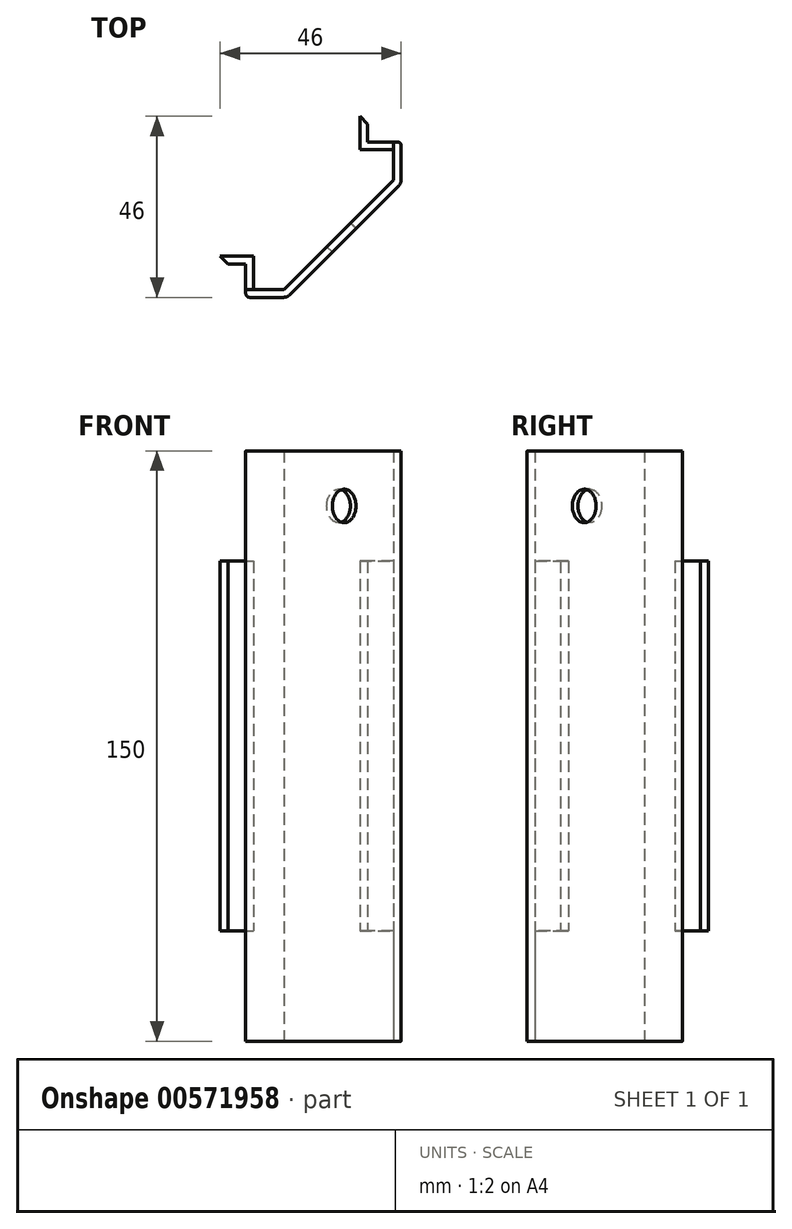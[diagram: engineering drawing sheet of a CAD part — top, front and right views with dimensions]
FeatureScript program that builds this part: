
annotation { "Feature Type Name" : "Feature", "Feature Type Description" : "" }
export const myFeature = defineFeature(function(context is Context, id is Id, definition is map)
    precondition{}
    {
        {
            var Q0;
            Q0=qCreatedBy(makeId("Top.planeOp"),FACE);
            var sketch = newSketch(context, id + "F0", { "sketchPlane" : qUnion([Q0])});
            skLineSegment(sketch, "E0", {"start": v(-68.1, 0) * mm, "end": v(72.16, 0) * mm, "construction": true});
            skLineSegment(sketch, "E1", {"start": v(0, 70.28) * mm, "end": v(0, -61.88) * mm, "construction": true});
            skLineSegment(sketch, "E2.bottom", {"start": v(-19.75, 19.75) * mm, "end": v(19.75, 19.75) * mm, "construction": true});
            skLineSegment(sketch, "E2.top", {"start": v(-19.75, -19.75) * mm, "end": v(19.75, -19.75) * mm, "construction": true});
            skLineSegment(sketch, "E2.left", {"start": v(-19.75, 19.75) * mm, "end": v(-19.75, -19.75) * mm, "construction": true});
            skLineSegment(sketch, "E2.right", {"start": v(19.75, 19.75) * mm, "end": v(19.75, -19.75) * mm, "construction": true});
            skLineSegment(sketch, "E3", {"start": v(-19.75, -19.75) * mm, "end": v(-9.25, -19.75) * mm});
            skLineSegment(sketch, "E4", {"start": v(19.75, 19.75) * mm, "end": v(19.75, 9.25) * mm});
            skLineSegment(sketch, "E5", {"start": v(-9.25, -19.75) * mm, "end": v(19.75, 9.25) * mm});
            skLineSegment(sketch, "E6.0", {"start": v(-19.75, -17.75) * mm, "end": v(-10.08, -17.75) * mm});
            skLineSegment(sketch, "E6.1", {"start": v(-10.08, -17.75) * mm, "end": v(17.75, 10.08) * mm});
            skLineSegment(sketch, "E6.2", {"start": v(17.75, 19.75) * mm, "end": v(17.75, 10.08) * mm});
            skLineSegment(sketch, "E7", {"start": v(-19.75, -19.75) * mm, "end": v(-19.75, -17.75) * mm});
            skLineSegment(sketch, "E8", {"start": v(19.75, 19.75) * mm, "end": v(17.75, 19.75) * mm});
            skSolve(sketch);
        }
        {
            var Q0;
            Q0=qSketchRegion(id+"F0",true);
            extrude(context, id + "F1", {"entities" : qUnion([Q0]), "depth" : 28 * mm});
        }
        {
            var Q0;
            Q0=makeQuery(id+"F1.opExtrude","CAP_FACE",FACE,{"disambiguationData":[OSD([sQuery(id+"F0.wireOp",EDGE,"E3"),sQuery(id+"F0.wireOp",EDGE,"E4"),sQuery(id+"F0.wireOp",EDGE,"E5"),sQuery(id+"F0.wireOp",EDGE,"E6.0"),sQuery(id+"F0.wireOp",EDGE,"E6.1"),sQuery(id+"F0.wireOp",EDGE,"E6.2"),sQuery(id+"F0.wireOp",EDGE,"E7"),sQuery(id+"F0.wireOp",EDGE,"E8")])],"isStart":false});
            var sketch = newSketch(context, id + "F2", { "sketchPlane" : qUnion([Q0])});
            skLineSegment(sketch, "E9.1", {"start": v(-9.25, -19.75) * mm, "end": v(19.75, 9.25) * mm});
            skLineSegment(sketch, "E9.2", {"start": v(19.75, 19.75) * mm, "end": v(19.75, 9.25) * mm});
            skLineSegment(sketch, "E10", {"start": v(19.75, 19.75) * mm, "end": v(11.25, 19.75) * mm});
            skLineSegment(sketch, "E11", {"start": v(17.75, 17.75) * mm, "end": v(17.75, 10.08) * mm});
            skLineSegment(sketch, "E12", {"start": v(17.75, 10.08) * mm, "end": v(16.59, 8.91) * mm});
            skLineSegment(sketch, "E13.left", {"start": v(11.25, 19.75) * mm, "end": v(11.25, 24.25) * mm});
            skLineSegment(sketch, "E14", {"start": v(11.25, 24.25) * mm, "end": v(9.25, 26.25) * mm});
            skLineSegment(sketch, "E15.trimOffspring", {"start": v(16.59, 8.91) * mm, "end": v(-8.91, -16.59) * mm});
            skLineSegment(sketch, "E16.0", {"start": v(9.25, 19.75) * mm, "end": v(9.25, 23.42) * mm});
            skLineSegment(sketch, "E17.0", {"start": v(9.25, 23.42) * mm, "end": v(9.25, 23.42) * mm});
            skLineSegment(sketch, "E18.trimOffspring", {"start": v(9.25, 23.42) * mm, "end": v(9.25, 26.25) * mm});
            skLineSegment(sketch, "E19", {"start": v(0, 0) * mm, "end": v(5.25, -5.25) * mm, "construction": true});
            skLineSegment(sketch, "E20.MirrorCS", {"start": v(-19.75, -9.25) * mm, "end": v(-23.42, -9.25) * mm});
            skLineSegment(sketch, "E21.MirrorCS", {"start": v(-19.75, -11.25) * mm, "end": v(-24.25, -11.25) * mm});
            skLineSegment(sketch, "E22.MirrorCS", {"start": v(-23.42, -9.25) * mm, "end": v(-26.25, -9.25) * mm});
            skLineSegment(sketch, "E23.MirrorCS", {"start": v(-19.75, -19.75) * mm, "end": v(-9.25, -19.75) * mm});
            skLineSegment(sketch, "E24.MirrorCS", {"start": v(-10.08, -17.75) * mm, "end": v(-8.91, -16.59) * mm});
            skLineSegment(sketch, "E25.MirrorCS", {"start": v(-24.25, -11.25) * mm, "end": v(-26.25, -9.25) * mm});
            skLineSegment(sketch, "E26.MirrorCS", {"start": v(-17.75, -17.75) * mm, "end": v(-10.08, -17.75) * mm});
            skLineSegment(sketch, "E27.MirrorCS", {"start": v(-23.42, -9.25) * mm, "end": v(-23.42, -9.25) * mm});
            skLineSegment(sketch, "E28.MirrorCS", {"start": v(-19.75, -19.75) * mm, "end": v(-19.75, -11.25) * mm});
            skLineSegment(sketch, "E29.trimOffspring", {"start": v(-8.91, -16.59) * mm, "end": v(-10.08, -17.75) * mm});
            skLineSegment(sketch, "E30", {"start": v(9.25, 19.75) * mm, "end": v(9.25, 17.75) * mm});
            skLineSegment(sketch, "E31", {"start": v(9.25, 17.75) * mm, "end": v(17.75, 17.75) * mm});
            skLineSegment(sketch, "E32", {"start": v(-19.75, -9.25) * mm, "end": v(-17.75, -9.25) * mm});
            skLineSegment(sketch, "E33", {"start": v(-17.75, -9.25) * mm, "end": v(-17.75, -17.75) * mm});
            skSolve(sketch);
        }
        {
            var Q0;
            Q0=qSketchRegion(id+"F2",true);
            extrude(context, id + "F3", {"entities" : qUnion([Q0]), "operationType" : NewBodyOperationType.ADD, "depth" : 94 * mm, "offsetDistance" : 25 * mm});
        }
        {
            var Q0;
            Q0=makeQuery(id+"F3.opExtrude","CAP_FACE",FACE,{"disambiguationData":[OSD([sQuery(id+"F2.wireOp",EDGE,"E9.1"),sQuery(id+"F2.wireOp",EDGE,"E9.2"),sQuery(id+"F2.wireOp",EDGE,"E10"),sQuery(id+"F2.wireOp",EDGE,"E11"),sQuery(id+"F2.wireOp",EDGE,"E12"),sQuery(id+"F2.wireOp",EDGE,"E13.left"),sQuery(id+"F2.wireOp",EDGE,"E14"),sQuery(id+"F2.wireOp",EDGE,"E15.trimOffspring"),sQuery(id+"F2.wireOp",EDGE,"E16.0"),sQuery(id+"F2.wireOp",EDGE,"E17.0"),sQuery(id+"F2.wireOp",EDGE,"E18.trimOffspring"),sQuery(id+"F2.wireOp",EDGE,"E20.MirrorCS"),sQuery(id+"F2.wireOp",EDGE,"E21.MirrorCS"),sQuery(id+"F2.wireOp",EDGE,"E22.MirrorCS"),sQuery(id+"F2.wireOp",EDGE,"E23.MirrorCS"),sQuery(id+"F2.wireOp",EDGE,"E25.MirrorCS"),sQuery(id+"F2.wireOp",EDGE,"E26.MirrorCS"),sQuery(id+"F2.wireOp",EDGE,"E27.MirrorCS"),sQuery(id+"F2.wireOp",EDGE,"E28.MirrorCS"),sQuery(id+"F2.wireOp",EDGE,"E29.trimOffspring"),sQuery(id+"F2.wireOp",EDGE,"E30"),sQuery(id+"F2.wireOp",EDGE,"E31"),sQuery(id+"F2.wireOp",EDGE,"E32"),sQuery(id+"F2.wireOp",EDGE,"E33")])],"isStart":false});
            var sketch = newSketch(context, id + "F4", { "sketchPlane" : qUnion([Q0])});
            skLineSegment(sketch, "E34.0.0", {"start": v(19.75, 19.75) * mm, "end": v(19.75, 9.25) * mm});
            skLineSegment(sketch, "E34.0.1", {"start": v(19.75, 9.25) * mm, "end": v(-9.25, -19.75) * mm});
            skLineSegment(sketch, "E34.0.2", {"start": v(-9.25, -19.75) * mm, "end": v(-19.75, -19.75) * mm});
            skLineSegment(sketch, "E34.0.3", {"start": v(-19.75, -19.75) * mm, "end": v(-19.75, -17.75) * mm});
            skLineSegment(sketch, "E34.0.4", {"start": v(-19.75, -17.75) * mm, "end": v(-10.08, -17.75) * mm});
            skLineSegment(sketch, "E34.0.5", {"start": v(-10.08, -17.75) * mm, "end": v(17.75, 10.08) * mm});
            skLineSegment(sketch, "E34.0.6", {"start": v(17.75, 10.08) * mm, "end": v(17.75, 19.75) * mm});
            skLineSegment(sketch, "E34.0.7", {"start": v(17.75, 19.75) * mm, "end": v(19.75, 19.75) * mm});
            skSolve(sketch);
        }
        {
            var Q0;
            Q0=qSketchRegion(id+"F4",true);
            extrude(context, id + "F5", {"entities" : qUnion([Q0]), "operationType" : NewBodyOperationType.ADD, "depth" : 28 * mm});
        }
        {
            var Q0;
            Q0=makeQuery(id+"F5.boolean.opBoolean","MERGE",EDGE,{"derivedFrom":[makeQuery(id+"F3.boolean.opBoolean","MERGE",EDGE,{"derivedFrom":[makeQuery(id+"F1.opExtrude","SWEPT_EDGE",EDGE,{"disambiguationData":[OSD([sQuery(id+"F0.wireOp",EDGE,"E4"),sQuery(id+"F0.wireOp",EDGE,"E5")])]}),makeQuery(id+"F3.opExtrude","SWEPT_EDGE",EDGE,{"disambiguationData":[OSD([sQuery(id+"F2.wireOp",EDGE,"E9.1"),sQuery(id+"F2.wireOp",EDGE,"E9.2")])]})]}),makeQuery(id+"F5.opExtrude","SWEPT_EDGE",EDGE,{"disambiguationData":[OSD([sQuery(id+"F4.wireOp",EDGE,"E34.0.0"),sQuery(id+"F4.wireOp",EDGE,"E34.0.1")])]})]});
            var Q1;
            Q1=makeQuery(id+"F5.boolean.opBoolean","MERGE",EDGE,{"derivedFrom":[makeQuery(id+"F3.boolean.opBoolean","MERGE",EDGE,{"derivedFrom":[makeQuery(id+"F1.opExtrude","SWEPT_EDGE",EDGE,{"disambiguationData":[OSD([sQuery(id+"F0.wireOp",EDGE,"E3"),sQuery(id+"F0.wireOp",EDGE,"E5")])]}),makeQuery(id+"F3.opExtrude","SWEPT_EDGE",EDGE,{"disambiguationData":[OSD([sQuery(id+"F2.wireOp",EDGE,"E9.1"),sQuery(id+"F2.wireOp",EDGE,"E23.MirrorCS")])]})]}),makeQuery(id+"F5.opExtrude","SWEPT_EDGE",EDGE,{"disambiguationData":[OSD([sQuery(id+"F4.wireOp",EDGE,"E34.0.1"),sQuery(id+"F4.wireOp",EDGE,"E34.0.2")])]})]});
            fillet(context, id + "F6", {"entities" : qUnion([Q0, Q1]), "radius" : 2 * mm, "tangentPropagation" : true, "allowEdgeOverflow" : false});
        }
        {
            var Q0;
            Q0=makeQuery(id+"F5.boolean.opBoolean","MERGE",EDGE,{"derivedFrom":[makeQuery(id+"F3.boolean.opBoolean","MERGE",EDGE,{"derivedFrom":[makeQuery(id+"F1.opExtrude","SWEPT_EDGE",EDGE,{"disambiguationData":[OSD([sQuery(id+"F0.wireOp",EDGE,"E3"),sQuery(id+"F0.wireOp",EDGE,"E7")])]}),makeQuery(id+"F3.opExtrude","SWEPT_EDGE",EDGE,{"disambiguationData":[OSD([sQuery(id+"F2.wireOp",EDGE,"E23.MirrorCS"),sQuery(id+"F2.wireOp",EDGE,"E28.MirrorCS")])]})]}),makeQuery(id+"F5.opExtrude","SWEPT_EDGE",EDGE,{"disambiguationData":[OSD([sQuery(id+"F4.wireOp",EDGE,"E34.0.2"),sQuery(id+"F4.wireOp",EDGE,"E34.0.3")])]})]});
            var Q1;
            Q1=makeQuery(id+"F5.boolean.opBoolean","MERGE",EDGE,{"derivedFrom":[makeQuery(id+"F3.boolean.opBoolean","MERGE",EDGE,{"derivedFrom":[makeQuery(id+"F1.opExtrude","SWEPT_EDGE",EDGE,{"disambiguationData":[OSD([sQuery(id+"F0.wireOp",EDGE,"E4"),sQuery(id+"F0.wireOp",EDGE,"E8")])]}),makeQuery(id+"F3.opExtrude","SWEPT_EDGE",EDGE,{"disambiguationData":[OSD([sQuery(id+"F2.wireOp",EDGE,"E9.2"),sQuery(id+"F2.wireOp",EDGE,"E10")])]})]}),makeQuery(id+"F5.opExtrude","SWEPT_EDGE",EDGE,{"disambiguationData":[OSD([sQuery(id+"F4.wireOp",EDGE,"E34.0.0"),sQuery(id+"F4.wireOp",EDGE,"E34.0.7")])]})]});
            fillet(context, id + "F7", {"entities" : qUnion([Q0, Q1]), "radius" : 1 * mm, "tangentPropagation" : true, "allowEdgeOverflow" : false});
        }
        {
            var Q0;
            Q0=makeQuery(id+"F5.boolean.opBoolean","MERGE",FACE,{"derivedFrom":[makeQuery(id+"F3.boolean.opBoolean","MERGE",FACE,{"derivedFrom":[makeQuery(id+"F1.opExtrude","SWEPT_FACE",FACE,{"disambiguationData":[OSD([sQuery(id+"F0.wireOp",EDGE,"E5")])]}),makeQuery(id+"F3.opExtrude","SWEPT_FACE",FACE,{"disambiguationData":[OSD([sQuery(id+"F2.wireOp",EDGE,"E9.1")])]})]}),makeQuery(id+"F5.opExtrude","SWEPT_FACE",FACE,{"disambiguationData":[OSD([sQuery(id+"F4.wireOp",EDGE,"E34.0.1")])]})]});
            var sketch = newSketch(context, id + "F8", { "sketchPlane" : qUnion([Q0])});
            skLineSegment(sketch, "E35.0", {"start": v(-19.1, 122) * mm, "end": v(-25.1, 122) * mm, "construction": true});
            skLineSegment(sketch, "E36", {"start": v(-19.1, 122) * mm, "end": v(27.6, 122) * mm, "construction": true});
            skLineSegment(sketch, "E37", {"start": v(0, 150) * mm, "end": v(0, 122) * mm, "construction": true});
            skCircle(sketch, "E38", {"center": v(0, 136) * mm, "radius": 4.25 * mm});
            skSolve(sketch);
        }
        {
            var Q0;
            Q0=qSketchRegion(id+"F8",true);
            extrude(context, id + "F9", {"entities" : qUnion([Q0]), "operationType" : NewBodyOperationType.REMOVE, "oppositeDirection" : true, "depth" : 25 * mm, "offsetDistance" : 25 * mm});
        }
    });
